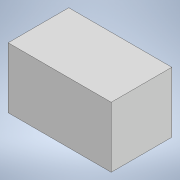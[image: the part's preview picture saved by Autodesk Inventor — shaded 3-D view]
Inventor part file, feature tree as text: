
AUTODESK INVENTOR PART (.ipt)
format: ipt  version: 2022 (Build 260153000, 153)  size: 85,504 bytes
history: native  units: mm
features: other x1, extrude x1, sketch x1
ambient origin geometry x8: Origin, YZ Plane, XZ Plane, XY Plane, X Axis, Y Axis, Z Axis, Center Point
bodies: Body1 (feature_tree)
feature tree (3):
  other  "Твердое тело1"
  extrude  "Выдавливание1"  Depth=100.0mm
  sketch  "Эскиз1"
